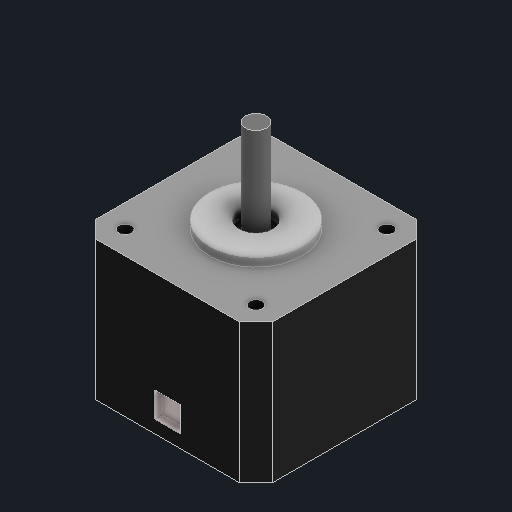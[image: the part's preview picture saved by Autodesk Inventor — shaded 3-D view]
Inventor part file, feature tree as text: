
AUTODESK INVENTOR PART (.ipt)
format: ipt  version: 2025.1 (Build 291241000, 241)  size: 270,848 bytes
history: native  units: mm
features: extrude x5, sketch x2
ambient origin geometry x8: Origin, YZ Plane, XZ Plane, XY Plane, X Axis, Y Axis, Z Axis, Center Point
bodies: Solid1 (feature_tree)
feature tree (7):
  sketch  "Sketch1"  dims[d1=31.0mm d2=31.0mm]
  extrude  "Extrusion1"  Depth=31.0mm
  extrude  "Extrusion2"  Depth=3.0mm
  extrude  "Extrusion3"  Depth=3.0mm
  extrude  "Extrusion4"  Depth=3.0mm
  extrude  "Extrusion5"  Depth=3.0mm
  sketch  "Sketch2"  dims[d3=31.0mm d4=31.0mm d5=3.0mm d6=3.0mm d7=3.0mm d8=3.0mm d9=33.0mm d10=0.0mm d11=22.0mm d12=2.0mm d13=0.0mm d14=8.0mm d15=2.0mm d16=0.0mm d17=6.0mm d18=6.0mm d22=2.0mm d23=0.0mm d32=5.0mm d33=20.0mm d34=2.0mm d35=0.0mm d36=0.0mm d37=15.5mm d38=42.0mm d39=42.0mm d40=15.5mm d41=21.0mm d42=21.0mm d43=34.0mm d44=34.0mm d45=135.0deg d46=3.0mm]
